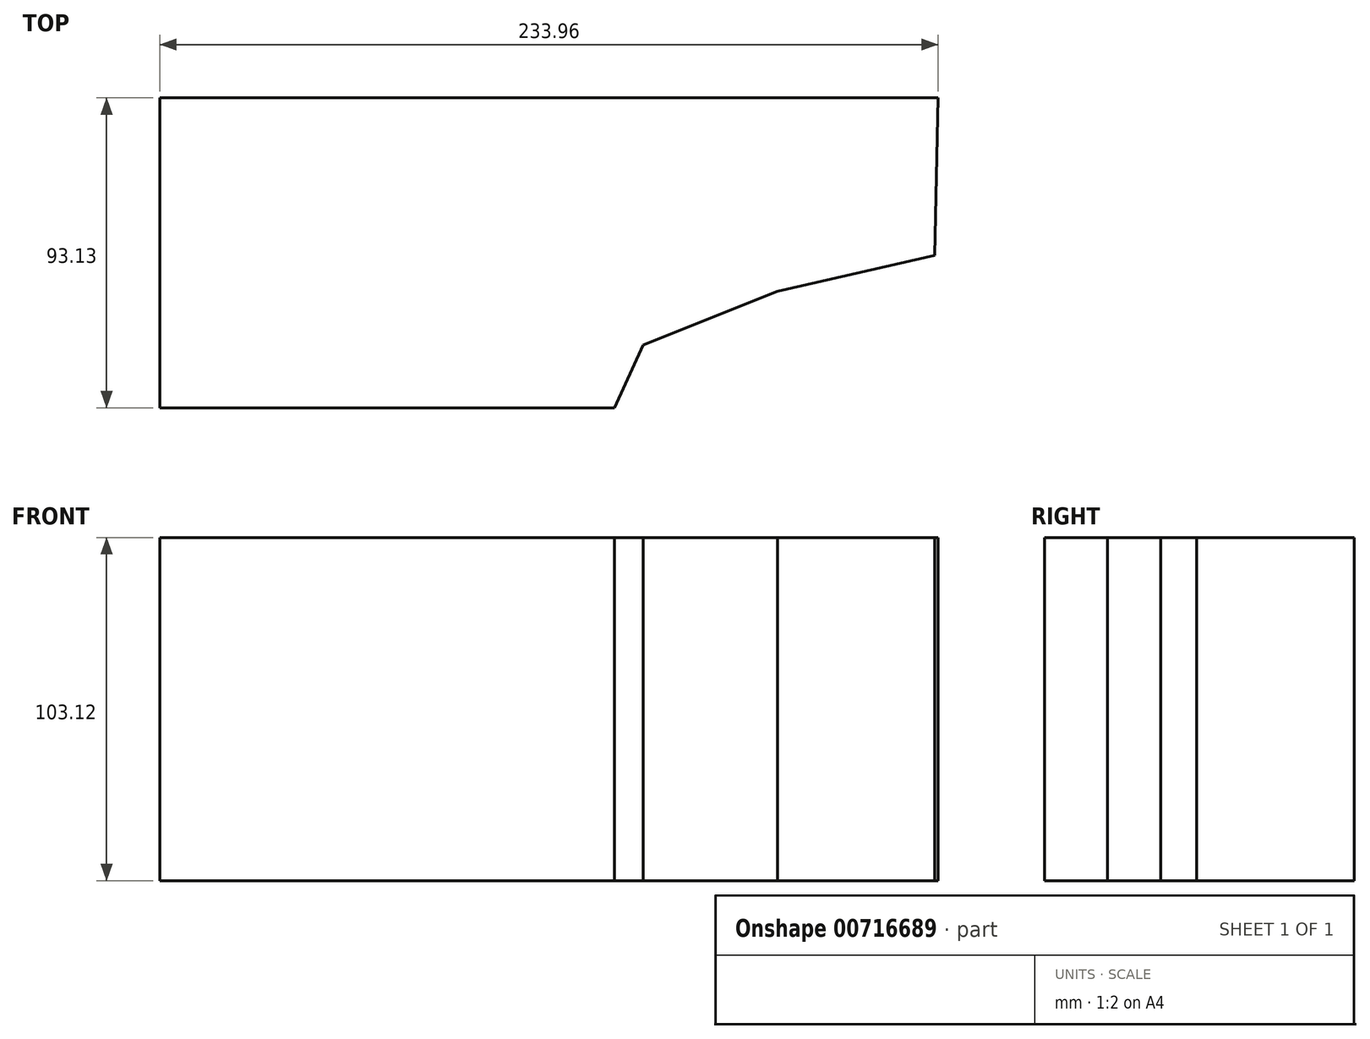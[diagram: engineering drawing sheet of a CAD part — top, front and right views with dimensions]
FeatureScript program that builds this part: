
annotation { "Feature Type Name" : "Feature", "Feature Type Description" : "" }
export const myFeature = defineFeature(function(context is Context, id is Id, definition is map)
    precondition{}
    {
        {
            var Q0;
            Q0=qCreatedBy(makeId("Top.planeOp"),FACE);
            var sketch = newSketch(context, id + "F0", { "sketchPlane" : qUnion([Q0])});
            skLineSegment(sketch, "E0", {"start": v(113.38, 47.4) * mm, "end": v(-120.58, 47.4) * mm});
            skLineSegment(sketch, "E1", {"start": v(-120.58, 47.4) * mm, "end": v(-120.58, -45.74) * mm});
            skLineSegment(sketch, "E2", {"start": v(-120.58, -45.74) * mm, "end": v(16.05, -45.74) * mm});
            skLineSegment(sketch, "E3", {"start": v(16.05, -45.74) * mm, "end": v(24.75, -26.85) * mm});
            skLineSegment(sketch, "E4", {"start": v(24.75, -26.85) * mm, "end": v(65.1, -10.8) * mm});
            skLineSegment(sketch, "E5", {"start": v(65.1, -10.8) * mm, "end": v(112.33, 0) * mm});
            skLineSegment(sketch, "E6", {"start": v(112.33, 0) * mm, "end": v(113.38, 47.4) * mm});
            skSolve(sketch);
        }
        {
            var Q0;
            Q0=makeQuery(id+"F0.imprint","IMPRINT",FACE,{"disambiguationData":[TD([[makeQuery(id+"F0.imprint","IMPRINT",EDGE,{"derivedFrom":sQuery(id+"F0.wireOp",EDGE,"E0")}),1.0]])]});
            extrude(context, id + "F1", {"entities" : qUnion([Q0]), "depth" : 103.12 * mm, "offsetDistance" : 25.4 * mm});
        }
    });
